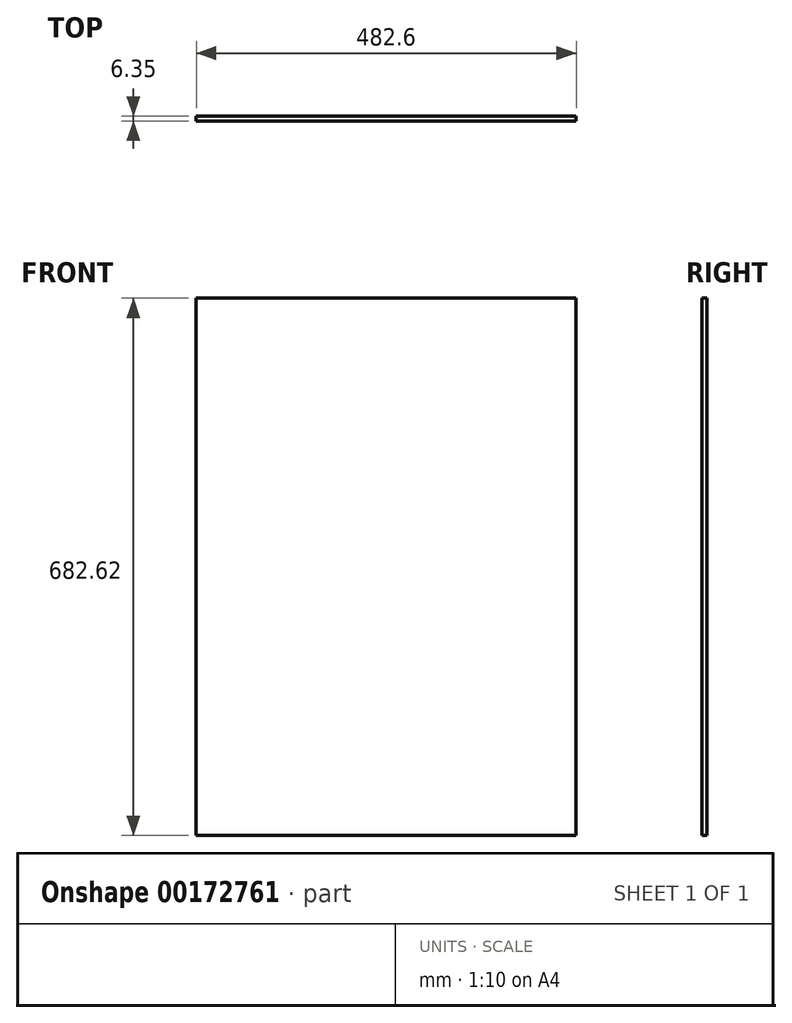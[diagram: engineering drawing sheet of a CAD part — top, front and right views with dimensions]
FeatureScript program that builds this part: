
annotation { "Feature Type Name" : "Feature", "Feature Type Description" : "" }
export const myFeature = defineFeature(function(context is Context, id is Id, definition is map)
    precondition{}
    {
        {
            var Q0;
            Q0=qCreatedBy(makeId("Front.planeOp"),FACE);
            var sketch = newSketch(context, id + "F0", { "sketchPlane" : qUnion([Q0])});
            skLineSegment(sketch, "E0.bottom", {"start": v(-238.5, 483.4) * mm, "end": v(244.1, 483.4) * mm});
            skLineSegment(sketch, "E0.top", {"start": v(-238.5, -199.23) * mm, "end": v(244.1, -199.23) * mm});
            skLineSegment(sketch, "E0.left", {"start": v(-238.5, 483.4) * mm, "end": v(-238.5, -199.23) * mm});
            skLineSegment(sketch, "E0.right", {"start": v(244.1, 483.4) * mm, "end": v(244.1, -199.23) * mm});
            skSolve(sketch);
        }
        {
            var Q0;
            Q0 = qSketchRegion(id + "F0", true);
            extrude(context, id + "F1", {"entities" : qUnion([Q0]), "depth" : 6.35 * mm});
        }
    });
